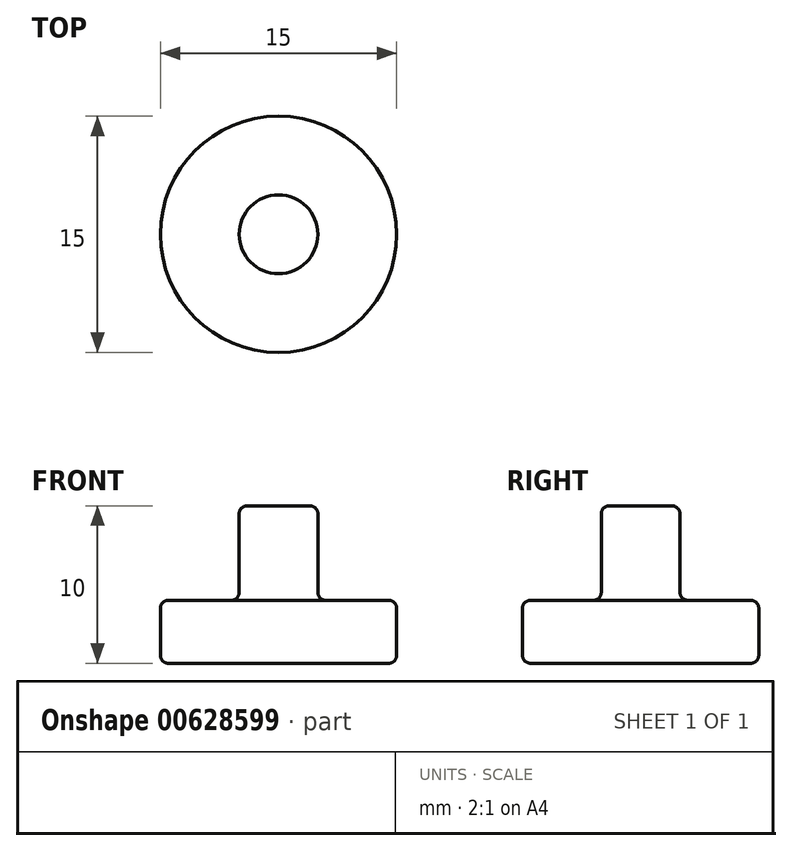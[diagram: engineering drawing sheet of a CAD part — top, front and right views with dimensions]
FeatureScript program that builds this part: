
annotation { "Feature Type Name" : "Feature", "Feature Type Description" : "" }
export const myFeature = defineFeature(function(context is Context, id is Id, definition is map)
    precondition{}
    {
        {
            var Q0;
            Q0=qCreatedBy(makeId("Top.planeOp"),FACE);
            var sketch = newSketch(context, id + "F0", { "sketchPlane" : qUnion([Q0])});
            skCircle(sketch, "E0", {"center": v(0, 0) * mm, "radius": 7.5 * mm});
            skCircle(sketch, "E1", {"center": v(0, 0) * mm, "radius": 2.5 * mm});
            skSolve(sketch);
        }
        {
            var Q0;
            Q0=makeQuery(id+"F0.imprint","IMPRINT",FACE,{"disambiguationData":[TD([[makeQuery(id+"F0.imprint","IMPRINT",EDGE,{"derivedFrom":sQuery(id+"F0.wireOp",EDGE,"E0")}),1.0]])]});
            var Q1;
            Q1=makeQuery(id+"F0.imprint","IMPRINT",FACE,{"disambiguationData":[TD([[makeQuery(id+"F0.imprint","IMPRINT",EDGE,{"derivedFrom":sQuery(id+"F0.wireOp",EDGE,"E1")}),1.0]])]});
            extrude(context, id + "F1", {"entities" : qUnion([Q0, Q1]), "depth" : 4 * mm, "offsetDistance" : 25 * mm});
        }
        {
            var Q0;
            Q0=makeQuery(id+"F0.imprint","IMPRINT",FACE,{"disambiguationData":[TD([[makeQuery(id+"F0.imprint","IMPRINT",EDGE,{"derivedFrom":sQuery(id+"F0.wireOp",EDGE,"E1")}),1.0]])]});
            extrude(context, id + "F2", {"entities" : qUnion([Q0]), "operationType" : NewBodyOperationType.ADD, "depth" : 10 * mm, "offsetDistance" : 25 * mm});
        }
        {
            var Q0;
            Q0=makeQuery(id+"F1.opExtrude","CAP_EDGE",EDGE,{"disambiguationData":[OSD([sQuery(id+"F0.wireOp",EDGE,"E0")])],"isStart":false});
            var Q1;
            Q1=makeQuery(id+"F1.opExtrude","CAP_EDGE",EDGE,{"disambiguationData":[OSD([sQuery(id+"F0.wireOp",EDGE,"E0")])],"isStart":true});
            var Q2;
            Q2=makeQuery(id+"F2.opExtrude","CAP_EDGE",EDGE,{"disambiguationData":[OSD([sQuery(id+"F0.wireOp",EDGE,"E1")])],"isStart":false});
            var Q3;
            Q3=makeQuery(id+"F2.boolean.opBoolean","INTERSECT",EDGE,{"derivedFrom":[makeQuery(id+"F1.opExtrude","CAP_FACE",FACE,{"disambiguationData":[OSD([sQuery(id+"F0.wireOp",EDGE,"E0")])],"isStart":false}),makeQuery(id+"F2.opExtrude","SWEPT_FACE",FACE,{"disambiguationData":[OSD([sQuery(id+"F0.wireOp",EDGE,"E1")])]})]});
            fillet(context, id + "F3", {"entities" : qUnion([Q0, Q1, Q2, Q3]), "radius" : .5 * mm, "tangentPropagation" : true, "allowEdgeOverflow" : false});
        }
    });
